# Revit family: BAS-IP_Блок бесперебойного питания_UPS-DP F
name_source: partatom
category: Устройства связи
units: mm (PartAtom-declared; Revit-internal decimal feet)

## family parameters
Всегда вертикально = Да
На основе рабочей плоскости = Нет
Общий = Нет
При загрузке вырезать с полостями = Нет
Размер круглого соединителя = Использовать диаметр
Сохранять ориентацию аннотаций = Нет
Тип детали = Нормальный
Точка расчета площади = Нет

## types (1)
- UPS-DP F
    ADSK_Единица измерения = шт.
    ADSK_Завод-изготовитель = BAS-IP
    ADSK_Количество = 1
    ADSK_Марка = UPS-DP/F
    ADSK_Материал = Black silver
    ADSK_Наименование = Блок бесперебойного питания
    Входное напряжение = AC 100-230 В
    Выходное напряжение = +12 В
    Габаритные размеры = 180 × 190 × 72 мм
    Изготовитель = BAS-IP
    Класс степени защиты = IP30C
    Корпус = Металлический
    Максимальный (кратковременный) ток нагрузки = 3,5 А
    Температурный режим = -40 – +60 °С
    Тип подключаемого оборудования = Многоабонентская вызывная панель
